# Revit family: P200921MX-068c_MVW7232H_CW
name_source: partatom
category: Specialty Equipment
units: mm (PartAtom-declared; Revit-internal decimal feet)

## family parameters
Always vertical = No
Cut with Voids When Loaded = No
Enable Cutting in Views = No
Maintain Annotation Orientation = No
Part Type = Normal
Room Calculation Point = No
Round Connector Dimension = Use Diameter
Shared = No
Work Plane-Based = No

## types (2) — shared parameters
Accent Material = ARCAT - Metal - Steel - Stainless
Amps = 0 A
Back Panel Material = ARCAT - Metal - Aluminum
Clearance Material = ARCAT - Clearance
Default Elevation = 0"
Depth = 27 7/8"
Description = Smart Capable Top Load Washer with Extra Power Button - 5.3 cu. ft.
Laveuse intelligente à chargement vertical, Extra Power, 5,3 pi³
Dimension Guide = https://www.whirlpool.com
https://www.whirlpool.com
Display Material = ARCAT - Glass - Tempered - Dark - Black
Display Panel Material = ARCAT - Metal - Steel - Dark - Gray
Energy Guide = https://www.whirlpool.com
https://www.whirlpool.com
Family Name = Laundry
Feature 1 = Most Powerful Cleaning in its class driven by the Heavy Duty cycle with Extra Power button
Most Powerful Cleaning in its class driven by the Heavy Duty cycle with Extra Power button
Feature 2 = Extra Power button
Extra Power button
Feature 3 = Smart capable appliance
Smart capable appliance
Glass Material = ARCAT - Glass - Tempered - Black
Handle Material = ARCAT - Metal - Steel - Stainless
Height = 42 7/8"
Knob Material = ARCAT - Metal - Steel - Stainless
Leg Material = ARCAT - Plastic - White
Manufacturer = Maytag
Voltage = 0 V
Width = 27 1/4"

## per-type parameters (varying)
| type | Body Material | Door Material |
| MVW7232HC | ARCAT - Metal - Steel - Gray | ARCAT - Metal - Steel - Gray |
| MVW7232HW | ARCAT - Metal - Steel - White | ARCAT - Metal - Steel - White |

note: column(s) folded — value = type name in every type: Model

## geometry (parser evidence)
native form markers: Sweep x5
no freeform markers — native parametric forms only
